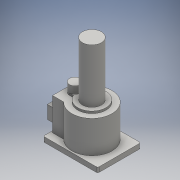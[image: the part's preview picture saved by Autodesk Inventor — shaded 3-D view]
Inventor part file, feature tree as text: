
AUTODESK INVENTOR PART (.ipt)
format: ipt  version: 2016 (Build 200138000, 138)  size: 162,816 bytes
history: native  units: mm
features: extrude x6, sketch x6, fillet x1
ambient origin geometry x8: Origin, YZ Plane, XZ Plane, XY Plane, X Axis, Y Axis, Z Axis, Center Point
bodies: Solid1 (feature_tree)
feature tree (13):
  extrude  "Extrusion1"  Depth=381.0mm
  fillet  "Fillet1"  Radius=43.2mm
  extrude  "Extrusion2"  Depth=12.7mm
  extrude  "Extrusion3"  Depth=248.0mm
  extrude  "Extrusion4"  Depth=238.0mm
  extrude  "Extrusion5"  Depth=74.2mm
  extrude  "Extrusion6"  Depth=479.0mm
  sketch  "Sketch1"  dims[d0=483.0mm d1=381.0mm d2=43.2mm d3=0.0mm]
  sketch  "Sketch2"  dims[d4=12.7mm d5=355.0mm]
  sketch  "Sketch3"  dims[d6=248.0mm d7=225.0mm]
  sketch  "Sketch4"  dims[d8=286.8mm d9=0.0mm d10=238.0mm]
  sketch  "Sketch5"  dims[d11=117.0mm d12=74.2mm]
  sketch  "Sketch6"  dims[d13=51.0mm d14=0.0mm d15=250.0mm d16=97.0mm d17=150.0mm d18=19.0mm d19=0.0mm d20=64.0mm d21=0.0mm d22=168.0mm d23=479.0mm d24=0.0mm]
